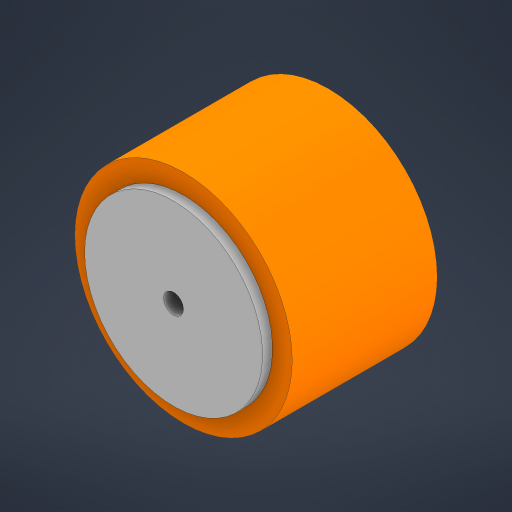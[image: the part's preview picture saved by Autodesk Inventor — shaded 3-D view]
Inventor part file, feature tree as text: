
AUTODESK INVENTOR PART (.ipt)
format: ipt  version: 2024 (Build 280153000, 153)  size: 274,944 bytes
history: native  units: mm
features: sketch x4, extrude x3, other x2, hole x2
ambient origin geometry x8: Origin, YZ Plane, XZ Plane, XY Plane, X Axis, Y Axis, Z Axis, Center Point
bodies: Body1 (feature_tree)
feature tree (11):
  other  "Těleso1"
  sketch  "Náčrt1"
  extrude  "Vysunutí1"  Depth=33.0mm
  hole  "Díra2"  [1 undecoded]
  other  "Závit1"
  extrude  "Vysunutí2"  Depth=25.0mm TaperAngle=0.0deg
  extrude  "Vysunutí3"  Depth=22.0mm TaperAngle=0.0deg
  hole  "Díra1"  [1 undecoded]
  sketch  "Náčrt2"
  sketch  "Náčrt3"
  sketch  "Náčrt4"
note: 2 required parameter values undecoded (feature->parameter linkage not recoverable at this tier; creation-order binding heuristic only, values carry confidence <= 0.55)
